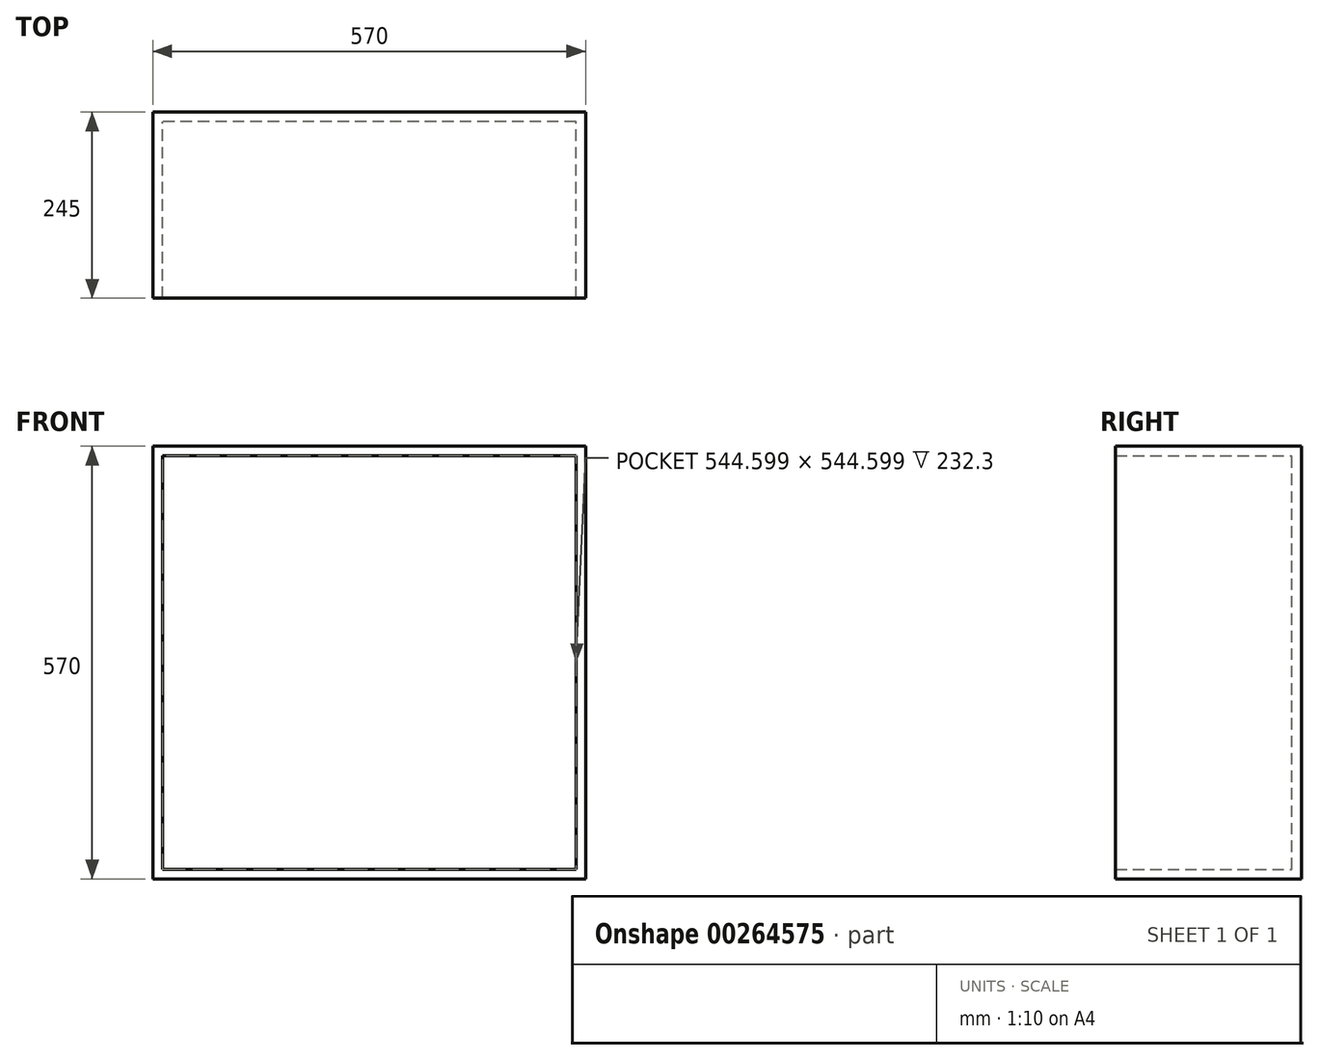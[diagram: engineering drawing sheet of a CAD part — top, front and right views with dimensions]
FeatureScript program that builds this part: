
annotation { "Feature Type Name" : "Feature", "Feature Type Description" : "" }
export const myFeature = defineFeature(function(context is Context, id is Id, definition is map)
    precondition{}
    {
        {
            var Q0;
            Q0=qCreatedBy(makeId("Front.planeOp"),FACE);
            var sketch = newSketch(context, id + "F0", { "sketchPlane" : qUnion([Q0])});
            skLineSegment(sketch, "E0.bottom", {"start": v(285, -285) * mm, "end": v(-285, -285) * mm});
            skLineSegment(sketch, "E0.top", {"start": v(285, 285) * mm, "end": v(-285, 285) * mm});
            skLineSegment(sketch, "E0.left", {"start": v(285, -285) * mm, "end": v(285, 285) * mm});
            skLineSegment(sketch, "E0.right", {"start": v(-285, -285) * mm, "end": v(-285, 285) * mm});
            skPoint(sketch, "E0.middle", {"position": v(0, 0) * mm});
            skSolve(sketch);
        }
        {
            var Q0;
            Q0 = qSketchRegion(id + "F0", true);
            extrude(context, id + "F1", {"entities" : qUnion([Q0]), "endBound" : BoundingType.SYMMETRIC, "depth" : 245 * mm});
        }
        {
            var Q0;
            Q0=makeQuery(id+"F1.opExtrude","CAP_FACE",FACE,{"disambiguationData":[OSD([sQuery(id+"F0.wireOp",EDGE,"E0.bottom"),sQuery(id+"F0.wireOp",EDGE,"E0.top"),sQuery(id+"F0.wireOp",EDGE,"E0.left"),sQuery(id+"F0.wireOp",EDGE,"E0.right")])],"isStart":false});
            shell(context, id + "F2", {"entities" : qUnion([Q0]), "thickness" : 12.7 * mm});
        }
    });
